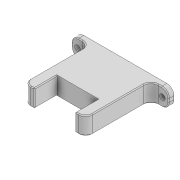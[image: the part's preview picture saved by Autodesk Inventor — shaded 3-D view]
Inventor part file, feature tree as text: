
AUTODESK INVENTOR PART (.ipt)
format: ipt  version: 2022 (Build 260153000, 153)  size: 224,768 bytes
history: native  units: mm
features: extrude x5, sketch x5, projected_geometry x5, other x1, fillet x1, chamfer x1
ambient origin geometry x8: Origin, YZ Plane, XZ Plane, XY Plane, X Axis, Y Axis, Z Axis, Center Point
bodies: Body1 (feature_tree)
feature tree (18):
  other  "Sólido1"
  extrude  "Extrusión1"  Depth=10.0mm
  extrude  "Extrusión2"  Depth=23.0mm
  extrude  "Extrusión3"  Depth=13.0mm TaperAngle=0.0deg
  fillet  "Empalme1"  Radius=10.0mm
  extrude  "Extrusión4"  Depth=3.0mm TaperAngle=0.0deg
  chamfer  "Chaflán1"  Distance=3.2mm
  extrude  "Extrusión5"  Depth=5.0mm
  sketch  "Boceto1"  dims[d0=35.0mm d1=10.0mm]
  sketch  "Boceto2"  dims[d2=40.0mm d3=0.0mm d4=23.0mm]
  projected_geometry  "Contorno proyectado1"
  sketch  "Boceto3"  dims[d5=11.5mm d6=13.0mm d7=0.0mm d8=10.0mm]
  projected_geometry  "Contorno proyectado2"
  sketch  "Boceto5"  dims[d9=10.0mm d12=3.0mm d13=0.0mm]
  projected_geometry  "Contorno proyectado5"
  projected_geometry  "Contorno proyectado6"
  sketch  "Boceto6"  dims[d14=4.0mm d15=3.2mm d16=3.2mm d17=3.5mm d18=3.5mm d19=10.0mm d20=0.0mm d21=0.5mm d22=2.0mm d23=45.0deg d26=28.0mm d27=14.0mm d28=6.2mm d29=3.5mm d30=3.5mm d31=5.0mm d32=0.0mm]
  projected_geometry  "Contorno proyectado7"
